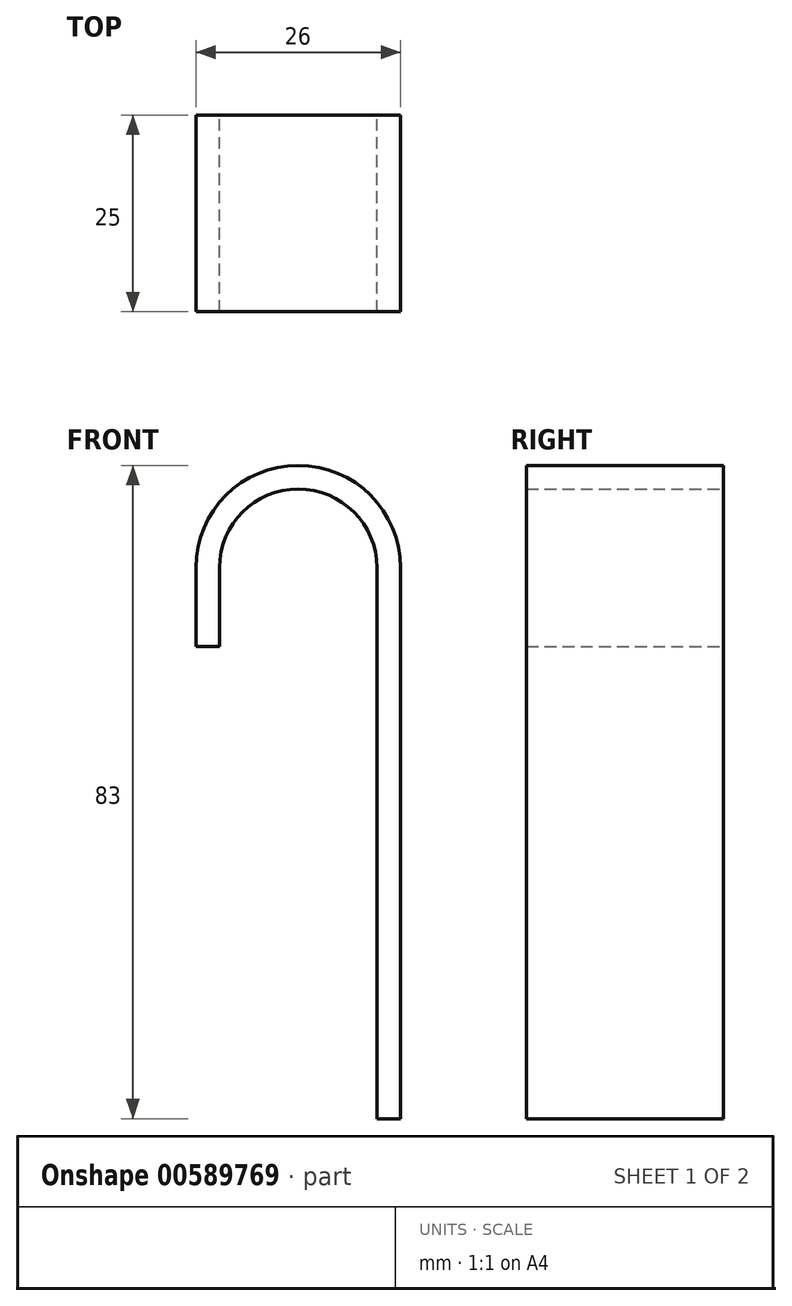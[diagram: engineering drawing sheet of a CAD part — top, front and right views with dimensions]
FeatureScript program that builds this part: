
annotation { "Feature Type Name" : "Feature", "Feature Type Description" : "" }
export const myFeature = defineFeature(function(context is Context, id is Id, definition is map)
    precondition{}
    {
        {
            var Q0;
            Q0=qCreatedBy(makeId("Front.planeOp"),FACE);
            var sketch = newSketch(context, id + "F0", { "sketchPlane" : qUnion([Q0])});
            skLineSegment(sketch, "E0.bottom", {"start": v(-1.5, 35) * mm, "end": v(1.5, 35) * mm});
            skLineSegment(sketch, "E0.top", {"start": v(-1.5, -35) * mm, "end": v(1.5, -35) * mm});
            skLineSegment(sketch, "E0.left", {"start": v(-1.5, 35) * mm, "end": v(-1.5, -35) * mm});
            skLineSegment(sketch, "E0.right", {"start": v(1.5, 35) * mm, "end": v(1.5, -35) * mm});
            skPoint(sketch, "E0.middle", {"position": v(0, 0) * mm});
            skArc(sketch, "E1", {"start": v(-1.5, 35) * mm, "mid": v(-11.5, 45) * mm, "end": v(-21.5, 35) * mm});
            skArc(sketch, "E2.0", {"start": v(1.5, 35) * mm, "mid": v(-11.5, 48) * mm, "end": v(-24.5, 35) * mm});
            skLineSegment(sketch, "E3", {"start": v(-24.5, 35) * mm, "end": v(-21.5, 35) * mm});
            skLineSegment(sketch, "E4", {"start": v(-24.5, 25) * mm, "end": v(-21.5, 25) * mm});
            skLineSegment(sketch, "E5", {"start": v(-21.5, 25) * mm, "end": v(-21.5, 35) * mm});
            skLineSegment(sketch, "E6", {"start": v(-24.5, 25) * mm, "end": v(-24.5, 35) * mm});
            skSolve(sketch);
        }
        {
            var Q0;
            Q0 = qSketchRegion(id + "F0", true);
            extrude(context, id + "F1", {"entities" : qUnion([Q0]), "depth" : 25 * mm, "offsetDistance" : 25 * mm});
        }
    });
